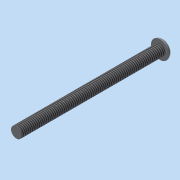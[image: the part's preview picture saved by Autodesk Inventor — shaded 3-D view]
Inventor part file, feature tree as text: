
AUTODESK INVENTOR PART (.ipt)
format: ipt  version: 2015 (Build 190159000, 159)  size: 89,088 bytes
history: native  units: mm
features: revolve x1, fillet x1, thread x1, sketch x1
ambient origin geometry x8: Origin, YZ Plane, XZ Plane, XY Plane, X Axis, Y Axis, Z Axis, Center Point
bodies: Solid1 (feature_tree)
feature tree (4):
  revolve  "Revolution1"  [1 undecoded]
  fillet  "Fillet1"  Radius=1.0mm
  thread  "Thread1"  [1 undecoded]
  sketch  "Sketch1"  dims[d0=1.5mm d1=2.5mm d2=1.0mm d3=90.0deg d4=1.0mm d5=10.0mm d6=0.0mm d7=40.0mm]
note: 2 required parameter values undecoded (feature->parameter linkage not recoverable at this tier; creation-order binding heuristic only, values carry confidence <= 0.55)